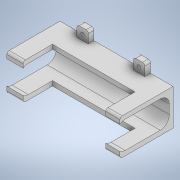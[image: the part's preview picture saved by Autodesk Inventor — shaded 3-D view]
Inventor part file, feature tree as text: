
AUTODESK INVENTOR PART (.ipt)
format: ipt  version: 2020 (Build 240168000, 168)  size: 216,576 bytes
history: native  units: in
note: dims shown in document units (in); Inventor stores cm internally (conversion verified against a paired STEP export)
features: sketch x5, extrude x4, plane x2, fillet x2
ambient origin geometry x8: Origin, YZ Plane, XZ Plane, XY Plane, X Axis, Y Axis, Z Axis, Center Point
bodies: Solid1 (feature_tree)
feature tree (13):
  sketch  "Sketch1"  dims[d1=1.8504in d2=0.0in d3=0.1969in d4=0.0in]
  extrude  "Extrusion1"  Depth=0.1969in TaperAngle=0.0deg
  extrude  "Extrusion2"  TaperAngle=0.0deg  [1 undecoded]
  plane  "Work Plane1"
  sketch  "Sketch3"  dims[d7=4.3307in d8=0.0in d9=1.5748in d10=0.0in]
  plane  "Work Plane2"
  extrude  "Extrusion3"  Depth=1.5748in TaperAngle=0.0deg
  extrude  "Extrusion4"  Depth=0.0787in
  fillet  "Fillet1"  [1 undecoded]
  fillet  "Fillet2"  [1 undecoded]
  sketch  "Sketch4"  dims[d11=0.0787in d12=0.0787in]
  sketch  "Sketch5"
  sketch  "Sketch2"  dims[d5=0.0in d6=0.0in]
note: 3 required parameter values undecoded (feature->parameter linkage not recoverable at this tier; creation-order binding heuristic only, values carry confidence <= 0.55)
